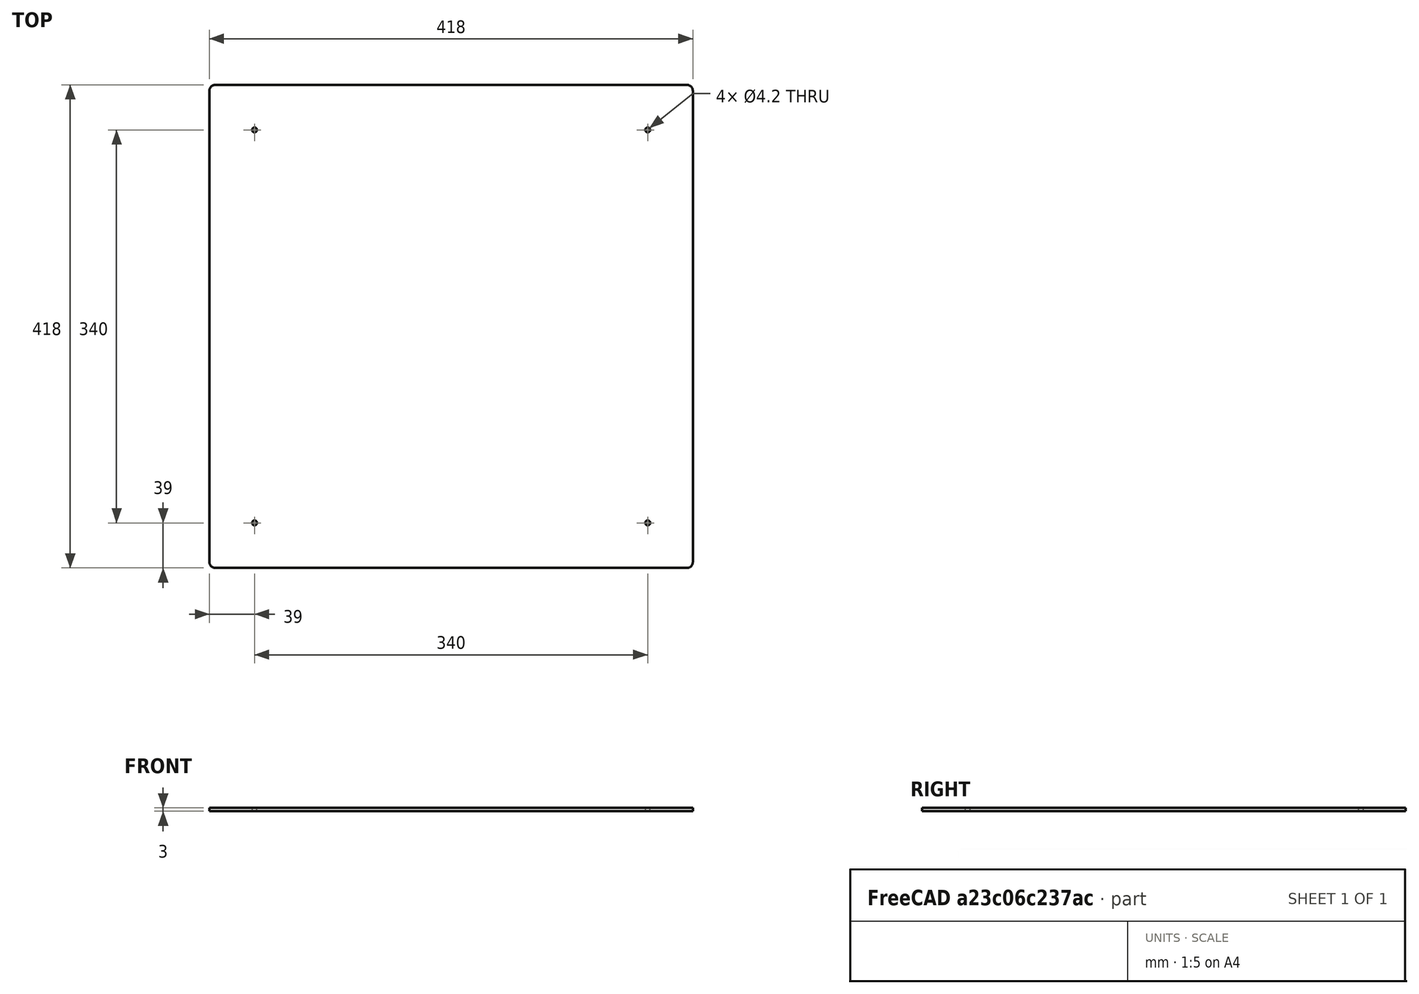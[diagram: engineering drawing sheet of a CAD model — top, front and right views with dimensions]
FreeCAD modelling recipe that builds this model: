
FCSTD DOCUMENT  (FreeCAD 0.19R20209 (Git))
Label: Alu-HeatBed-001
License: Creative Commons Attribution
LicenseURL: http://creativecommons.org/licenses/by/4.0/
objects: Sketcher::SketchObject×1, PartDesign::Pad×1, PartDesign::Body×1
note: 4 computed .brp shape members not serialized (recipe doc carries the construction recipe); baked Part::Feature solids carry a one-line shape summary decoded from their .brp

FEATURE [Sketcher::SketchObject] Sketch
  MapMode = 5
  Support = -> [XY_Plane]
  sketch-geometry (20):
    g0: LineSegment StartX=-204 StartY=209 StartZ=0 EndX=204 EndY=209 EndZ=0
    g1: LineSegment StartX=209 StartY=204 StartZ=0 EndX=209 EndY=-204 EndZ=0
    g2: LineSegment StartX=204 StartY=-209 StartZ=0 EndX=-204 EndY=-209 EndZ=0
    g3: LineSegment StartX=-209 StartY=-204 StartZ=0 EndX=-209 EndY=204 EndZ=0
    g4: LineSegment [constr] StartX=-170 StartY=170 StartZ=0 EndX=170 EndY=170 EndZ=0
    g5: LineSegment [constr] StartX=170 StartY=170 StartZ=0 EndX=170 EndY=-170 EndZ=0
    g6: LineSegment [constr] StartX=170 StartY=-170 StartZ=0 EndX=-170 EndY=-170 EndZ=0
    g7: LineSegment [constr] StartX=-170 StartY=-170 StartZ=0 EndX=-170 EndY=170 EndZ=0
    g8: Circle CenterX=-170 CenterY=170 CenterZ=0 NormalX=0 NormalY=0 NormalZ=1 AngleXU=0 Radius=2.1
    g9: Circle CenterX=170 CenterY=170 CenterZ=0 NormalX=0 NormalY=0 NormalZ=1 AngleXU=0 Radius=2.1
    g10: Circle CenterX=170 CenterY=-170 CenterZ=0 NormalX=0 NormalY=0 NormalZ=1 AngleXU=0 Radius=2.1
    g11: Circle CenterX=-170 CenterY=-170 CenterZ=0 NormalX=0 NormalY=0 NormalZ=1 AngleXU=0 Radius=2.1
    g12: ArcOfCircle CenterX=-204 CenterY=204 CenterZ=0 NormalX=0 NormalY=0 NormalZ=1 AngleXU=0 Radius=5 StartAngle=1.5708 EndAngle=3.14159
    g13: ArcOfCircle CenterX=204 CenterY=204 CenterZ=0 NormalX=0 NormalY=0 NormalZ=1 AngleXU=0 Radius=5 StartAngle=-2.7e-15 EndAngle=1.5708
    g14: ArcOfCircle CenterX=204 CenterY=-204 CenterZ=0 NormalX=0 NormalY=0 NormalZ=1 AngleXU=0 Radius=5 StartAngle=4.71239 EndAngle=6.28319
    g15: ArcOfCircle CenterX=-204 CenterY=-204 CenterZ=0 NormalX=0 NormalY=0 NormalZ=1 AngleXU=0 Radius=5 StartAngle=3.14159 EndAngle=4.71239
    g16: LineSegment [constr] StartX=-204 StartY=204 StartZ=0 EndX=204 EndY=204 EndZ=0
    g17: LineSegment [constr] StartX=204 StartY=204 StartZ=0 EndX=204 EndY=-204 EndZ=0
    g18: LineSegment [constr] StartX=204 StartY=-204 StartZ=0 EndX=-204 EndY=-204 EndZ=0
    g19: LineSegment [constr] StartX=-204 StartY=-204 StartZ=0 EndX=-204 EndY=204 EndZ=0
  constraints (51):
    c: Horizontal(g0)
    c: Horizontal(g2)
    c: Vertical(g1)
    c: Vertical(g3)
    c: Equal(g0,g3)
    c: Coincident(g4,g5)
    c: Coincident(g5,g6)
    c: Coincident(g6,g7)
    c: Coincident(g7,g4)
    c: Horizontal(g4)
    c: Horizontal(g6)
    c: Vertical(g5)
    c: Vertical(g7)
    c: Equal(g4,g7)
    c: DistanceX(g4,g4) = 340
    c: Symmetric(g4,g5,g-1)
    c: Equal(g8,g11)
    c: Equal(g11,g10)
    c: Equal(g10,g9)
    c: Coincident(g8,g4)
    c: Coincident(g9,g4)
    c: Coincident(g10,g5)
    c: Coincident(g11,g6)
    c: Tangent(g0,g12) = 1.5708
    c: Tangent(g3,g12) = 1.5708
    c: Tangent(g0,g13) = 1.5708
    c: Tangent(g1,g13) = 1.5708
    c: Tangent(g1,g14) = 1.5708
    c: Tangent(g2,g14) = 1.5708
    c: Tangent(g2,g15) = 1.5708
    c: Tangent(g3,g15) = 1.5708
    c: Coincident(g16,g17)
    c: Coincident(g17,g18)
    c: Coincident(g18,g19)
    c: Coincident(g19,g16)
    c: Horizontal(g16)
    c: Horizontal(g18)
    c: Vertical(g17)
    c: Vertical(g19)
    c: Symmetric(g17,g16,g-1)
    c: Equal(g16,g19)
    c: DistanceX(g16,g16) = 408
    c: Equal(g12,g13)
    c: Equal(g13,g14)
    c: Equal(g14,g15)
    c: Equal(g3,g0)
    c: Symmetric(g12,g14,g-1)
    c: Coincident(g12,g16)
    c: Diameter(g8) = 4.2
    c: DistanceX(g3,g1) = 418
    c: Radius(g12) = 5
FEATURE [PartDesign::Pad] Pad
  Length = 3
  Length2 = 100
  Profile = -> Sketch
  Refine = true
  Type = 0
FEATURE [PartDesign::Body] Body
  Group = -> [Sketch,Pad]
  Origin = -> Origin
  Tip = -> Pad
